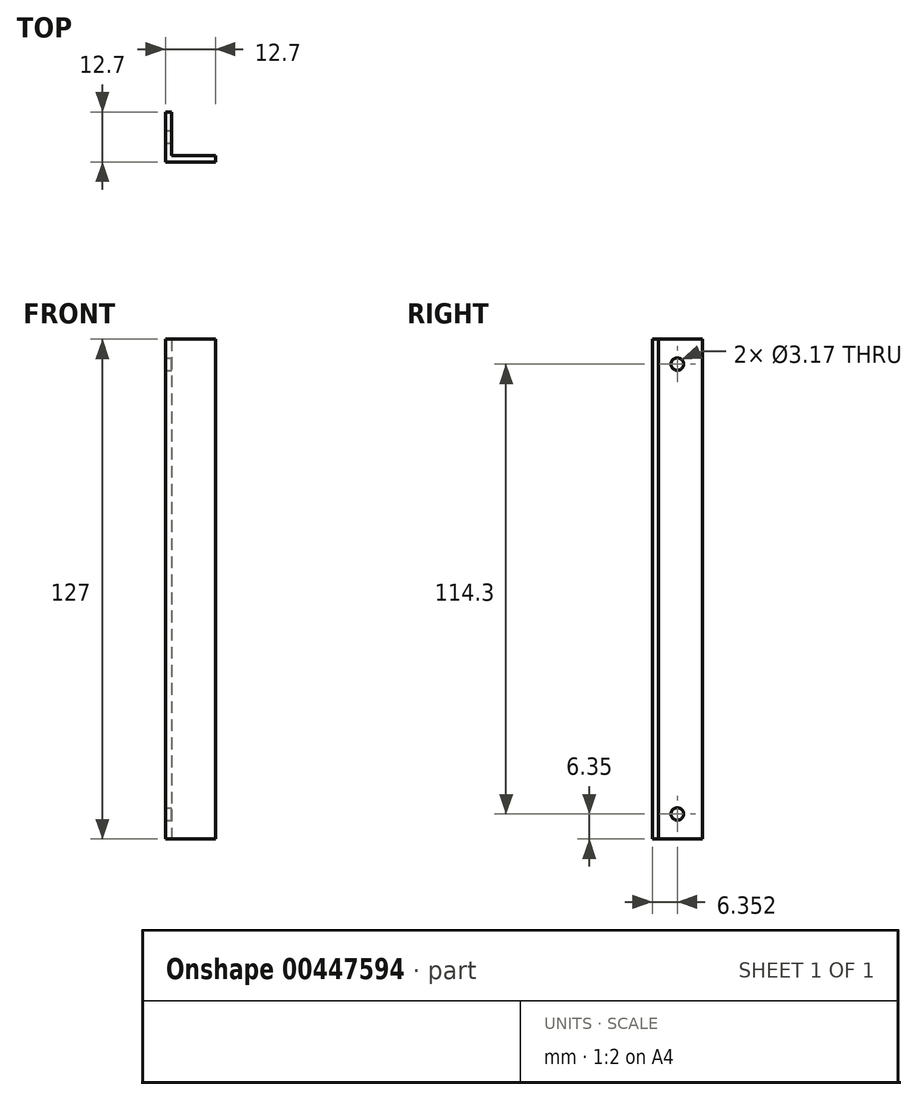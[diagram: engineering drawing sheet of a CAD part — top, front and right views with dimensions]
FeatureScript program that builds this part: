
annotation { "Feature Type Name" : "Feature", "Feature Type Description" : "" }
export const myFeature = defineFeature(function(context is Context, id is Id, definition is map)
    precondition{}
    {
        {
            var Q0;
            Q0=qCreatedBy(makeId("Top.planeOp"),FACE);
            var sketch = newSketch(context, id + "F0", { "sketchPlane" : qUnion([Q0])});
            skLineSegment(sketch, "E0", {"start": v(-18.8, -0.43) * mm, "end": v(-18.8, -13.13) * mm});
            skLineSegment(sketch, "E1", {"start": v(-18.8, -13.13) * mm, "end": v(-6.1, -13.13) * mm});
            skLineSegment(sketch, "E2", {"start": v(-18.8, -0.43) * mm, "end": v(-17.2, -0.43) * mm});
            skLineSegment(sketch, "E3", {"start": v(-6.1, -13.13) * mm, "end": v(-6.1, -11.54) * mm});
            skLineSegment(sketch, "E4", {"start": v(-17.2, -0.43) * mm, "end": v(-17.2, -11.54) * mm});
            skLineSegment(sketch, "E5", {"start": v(-17.2, -11.54) * mm, "end": v(-6.1, -11.54) * mm});
            skSolve(sketch);
        }
        {
            var Q0;
            Q0=makeQuery(id+"F0.imprint","IMPRINT",FACE,{"disambiguationData":[TD([[makeQuery(id+"F0.imprint","IMPRINT",EDGE,{"derivedFrom":sQuery(id+"F0.wireOp",EDGE,"E0")}),1.0]])]});
            extrude(context, id + "F1", {"entities" : qUnion([Q0]), "depth" : 127 * mm});
        }
        {
            var Q0;
            Q0=makeQuery(id+"F1.opExtrude","SWEPT_FACE",FACE,{"disambiguationData":[OSD([sQuery(id+"F0.wireOp",EDGE,"E5")])]});
            var sketch = newSketch(context, id + "F2", { "sketchPlane" : qUnion([Q0])});
            skSolve(sketch);
        }
        {
            var Q0;
            Q0=makeQuery(id+"F1.opExtrude","SWEPT_FACE",FACE,{"disambiguationData":[OSD([sQuery(id+"F0.wireOp",EDGE,"E4")])]});
            var sketch = newSketch(context, id + "F3", { "sketchPlane" : qUnion([Q0])});
            skCircle(sketch, "E6", {"center": v(-6.78, 6.35) * mm, "radius": 1.59 * mm});
            skCircle(sketch, "E7", {"center": v(-6.78, 120.65) * mm, "radius": 1.59 * mm});
            skSolve(sketch);
        }
        {
            var Q0;
            Q0=makeQuery(id+"F3.imprint","IMPRINT",FACE,{"disambiguationData":[TD([[makeQuery(id+"F3.imprint","IMPRINT",EDGE,{"derivedFrom":sQuery(id+"F3.wireOp",EDGE,"E6")}),1.0]])]});
            var Q1;
            Q1=makeQuery(id+"F3.imprint","IMPRINT",FACE,{"disambiguationData":[TD([[makeQuery(id+"F3.imprint","IMPRINT",EDGE,{"derivedFrom":sQuery(id+"F3.wireOp",EDGE,"E7")}),1.0]])]});
            extrude(context, id + "F4", {"entities" : qUnion([Q0, Q1]), "operationType" : NewBodyOperationType.REMOVE, "oppositeDirection" : true, "depth" : 25.4 * mm});
        }
    });
